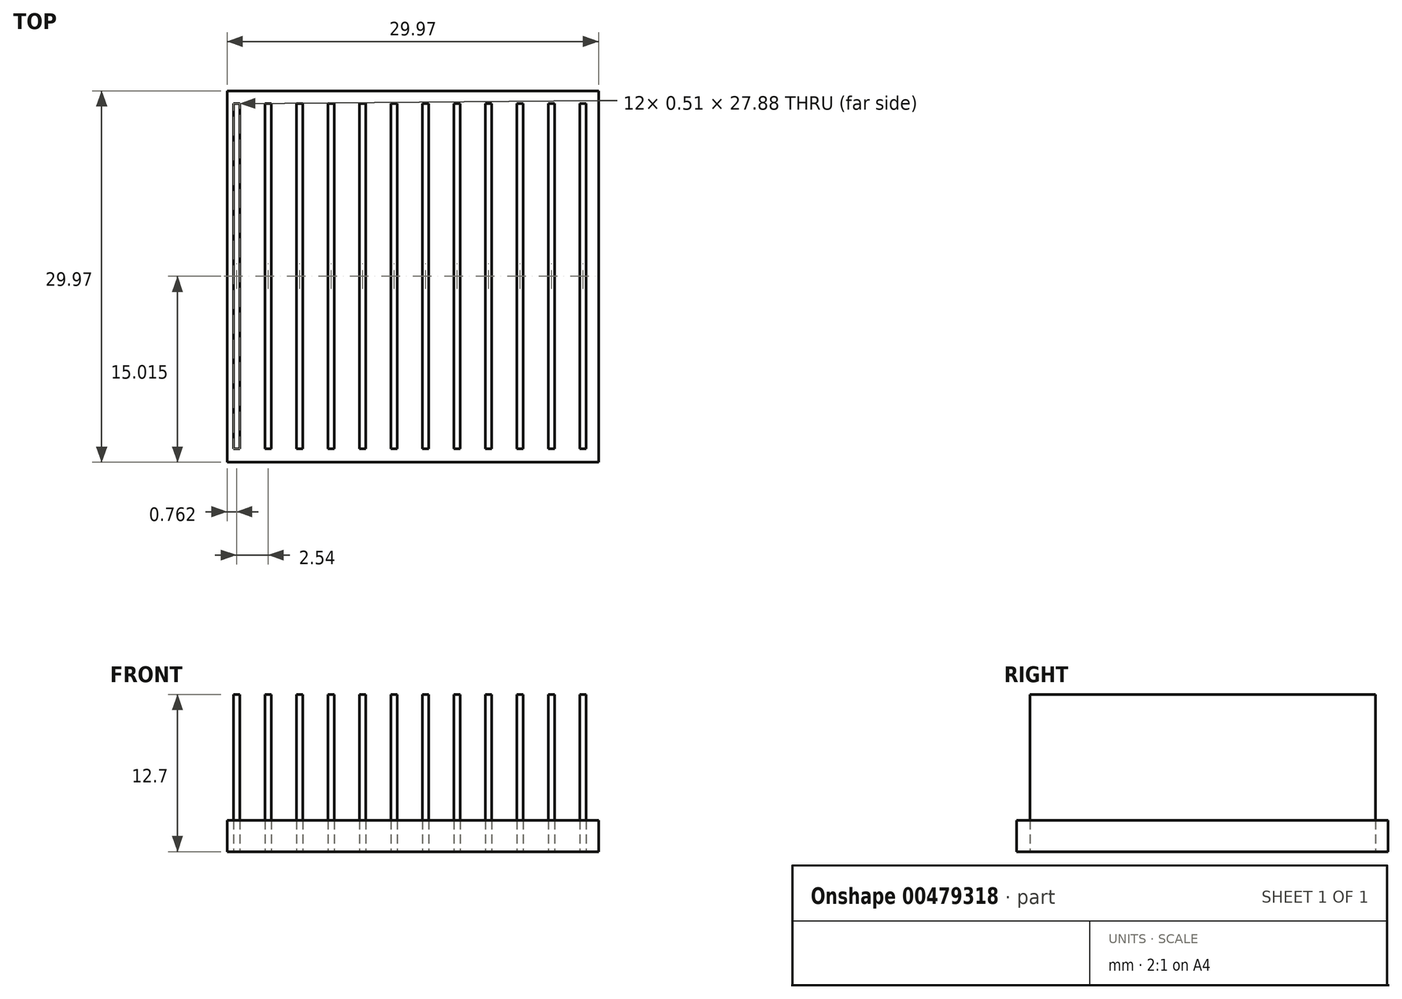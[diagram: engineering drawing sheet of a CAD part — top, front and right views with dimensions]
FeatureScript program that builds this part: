
annotation { "Feature Type Name" : "Feature", "Feature Type Description" : "" }
export const myFeature = defineFeature(function(context is Context, id is Id, definition is map)
    precondition{}
    {
        {
            var Q0;
            Q0=qCreatedBy(makeId("Top.planeOp"),FACE);
            var sketch = newSketch(context, id + "F0", { "sketchPlane" : qUnion([Q0])});
            skLineSegment(sketch, "E0.bottom", {"start": v(0, 0) * mm, "end": v(29.97, 0) * mm});
            skLineSegment(sketch, "E0.top", {"start": v(0, 29.97) * mm, "end": v(29.97, 29.97) * mm});
            skLineSegment(sketch, "E0.left", {"start": v(0, 0) * mm, "end": v(0, 29.97) * mm});
            skLineSegment(sketch, "E0.right", {"start": v(29.97, 0) * mm, "end": v(29.97, 29.97) * mm});
            skLineSegment(sketch, "E1.bottom", {"start": v(0.5, 28.96) * mm, "end": v(1.02, 28.96) * mm});
            skLineSegment(sketch, "E1.top", {"start": v(0.5, 1.07) * mm, "end": v(1.02, 1.07) * mm});
            skLineSegment(sketch, "E1.left", {"start": v(0.5, 28.96) * mm, "end": v(0.5, 1.07) * mm});
            skLineSegment(sketch, "E1.right", {"start": v(1.02, 28.96) * mm, "end": v(1.02, 1.07) * mm});
            skLineSegment(sketch, "E2.1.0.0", {"start": v(3.56, 28.96) * mm, "end": v(3.56, 1.07) * mm});
            skLineSegment(sketch, "E2.1.0.1", {"start": v(3.05, 28.96) * mm, "end": v(3.05, 1.07) * mm});
            skLineSegment(sketch, "E2.1.0.2", {"start": v(3.05, 1.07) * mm, "end": v(3.56, 1.07) * mm});
            skLineSegment(sketch, "E2.1.0.3", {"start": v(3.05, 28.96) * mm, "end": v(3.56, 28.96) * mm});
            skLineSegment(sketch, "E2.2.0.0", {"start": v(6.1, 28.96) * mm, "end": v(6.1, 1.07) * mm});
            skLineSegment(sketch, "E2.2.0.1", {"start": v(5.59, 28.96) * mm, "end": v(5.59, 1.07) * mm});
            skLineSegment(sketch, "E2.2.0.2", {"start": v(5.59, 1.07) * mm, "end": v(6.1, 1.07) * mm});
            skLineSegment(sketch, "E2.2.0.3", {"start": v(5.59, 28.96) * mm, "end": v(6.1, 28.96) * mm});
            skLineSegment(sketch, "E2.3.0.0", {"start": v(8.64, 28.96) * mm, "end": v(8.64, 1.07) * mm});
            skLineSegment(sketch, "E2.3.0.1", {"start": v(8.13, 28.96) * mm, "end": v(8.13, 1.07) * mm});
            skLineSegment(sketch, "E2.3.0.2", {"start": v(8.13, 1.07) * mm, "end": v(8.64, 1.07) * mm});
            skLineSegment(sketch, "E2.3.0.3", {"start": v(8.13, 28.96) * mm, "end": v(8.64, 28.96) * mm});
            skLineSegment(sketch, "E2.4.0.0", {"start": v(11.18, 28.96) * mm, "end": v(11.18, 1.07) * mm});
            skLineSegment(sketch, "E2.4.0.1", {"start": v(10.67, 28.96) * mm, "end": v(10.67, 1.07) * mm});
            skLineSegment(sketch, "E2.4.0.2", {"start": v(10.67, 1.07) * mm, "end": v(11.18, 1.07) * mm});
            skLineSegment(sketch, "E2.4.0.3", {"start": v(10.67, 28.96) * mm, "end": v(11.18, 28.96) * mm});
            skLineSegment(sketch, "E2.5.0.0", {"start": v(13.72, 28.96) * mm, "end": v(13.72, 1.07) * mm});
            skLineSegment(sketch, "E2.5.0.1", {"start": v(13.2, 28.96) * mm, "end": v(13.2, 1.07) * mm});
            skLineSegment(sketch, "E2.5.0.2", {"start": v(13.2, 1.07) * mm, "end": v(13.72, 1.07) * mm});
            skLineSegment(sketch, "E2.5.0.3", {"start": v(13.2, 28.96) * mm, "end": v(13.72, 28.96) * mm});
            skLineSegment(sketch, "E2.6.0.0", {"start": v(16.26, 28.96) * mm, "end": v(16.26, 1.07) * mm});
            skLineSegment(sketch, "E2.6.0.1", {"start": v(15.75, 28.96) * mm, "end": v(15.75, 1.07) * mm});
            skLineSegment(sketch, "E2.6.0.2", {"start": v(15.75, 1.07) * mm, "end": v(16.26, 1.07) * mm});
            skLineSegment(sketch, "E2.6.0.3", {"start": v(15.75, 28.96) * mm, "end": v(16.26, 28.96) * mm});
            skLineSegment(sketch, "E2.7.0.0", {"start": v(18.8, 28.96) * mm, "end": v(18.8, 1.07) * mm});
            skLineSegment(sketch, "E2.7.0.1", {"start": v(18.29, 28.96) * mm, "end": v(18.29, 1.07) * mm});
            skLineSegment(sketch, "E2.7.0.2", {"start": v(18.29, 1.07) * mm, "end": v(18.8, 1.07) * mm});
            skLineSegment(sketch, "E2.7.0.3", {"start": v(18.29, 28.96) * mm, "end": v(18.8, 28.96) * mm});
            skLineSegment(sketch, "E2.8.0.0", {"start": v(21.34, 28.96) * mm, "end": v(21.34, 1.07) * mm});
            skLineSegment(sketch, "E2.8.0.1", {"start": v(20.83, 28.96) * mm, "end": v(20.83, 1.07) * mm});
            skLineSegment(sketch, "E2.8.0.2", {"start": v(20.83, 1.07) * mm, "end": v(21.34, 1.07) * mm});
            skLineSegment(sketch, "E2.8.0.3", {"start": v(20.83, 28.96) * mm, "end": v(21.34, 28.96) * mm});
            skLineSegment(sketch, "E2.9.0.0", {"start": v(23.88, 28.96) * mm, "end": v(23.88, 1.07) * mm});
            skLineSegment(sketch, "E2.9.0.1", {"start": v(23.37, 28.96) * mm, "end": v(23.37, 1.07) * mm});
            skLineSegment(sketch, "E2.9.0.2", {"start": v(23.37, 1.07) * mm, "end": v(23.88, 1.07) * mm});
            skLineSegment(sketch, "E2.9.0.3", {"start": v(23.37, 28.96) * mm, "end": v(23.88, 28.96) * mm});
            skLineSegment(sketch, "E2.direction1", {"start": v(1.02, 1.07) * mm, "end": v(3.56, 1.07) * mm, "construction": true});
            skLineSegment(sketch, "E3.1.0.0", {"start": v(25.9, 28.96) * mm, "end": v(25.9, 1.07) * mm});
            skLineSegment(sketch, "E3.1.0.1", {"start": v(26.42, 28.96) * mm, "end": v(26.42, 1.07) * mm});
            skLineSegment(sketch, "E3.1.0.2", {"start": v(25.9, 1.07) * mm, "end": v(26.42, 1.07) * mm});
            skLineSegment(sketch, "E3.1.0.3", {"start": v(25.9, 28.96) * mm, "end": v(26.42, 28.96) * mm});
            skLineSegment(sketch, "E3.2.0.0", {"start": v(28.45, 28.96) * mm, "end": v(28.45, 1.07) * mm});
            skLineSegment(sketch, "E3.2.0.1", {"start": v(28.96, 28.96) * mm, "end": v(28.96, 1.07) * mm});
            skLineSegment(sketch, "E3.2.0.2", {"start": v(28.45, 1.07) * mm, "end": v(28.96, 1.07) * mm});
            skLineSegment(sketch, "E3.2.0.3", {"start": v(28.45, 28.96) * mm, "end": v(28.96, 28.96) * mm});
            skLineSegment(sketch, "E3.direction1", {"start": v(23.37, 1.07) * mm, "end": v(25.9, 1.07) * mm, "construction": true});
            skSolve(sketch);
        }
        {
            var Q0;
            Q0=makeQuery(id+"F0.imprint","IMPRINT",FACE,{"disambiguationData":[TD([[makeQuery(id+"F0.imprint","IMPRINT",EDGE,{"derivedFrom":sQuery(id+"F0.wireOp",EDGE,"E1.bottom")}),-1.0]])]});
            var Q1;
            Q1=makeQuery(id+"F0.imprint","IMPRINT",FACE,{"disambiguationData":[TD([[makeQuery(id+"F0.imprint","IMPRINT",EDGE,{"derivedFrom":sQuery(id+"F0.wireOp",EDGE,"E2.1.0.0")}),-1.0]])]});
            var Q2;
            Q2=makeQuery(id+"F0.imprint","IMPRINT",FACE,{"disambiguationData":[TD([[makeQuery(id+"F0.imprint","IMPRINT",EDGE,{"derivedFrom":sQuery(id+"F0.wireOp",EDGE,"E2.2.0.0")}),-1.0]])]});
            var Q3;
            Q3=makeQuery(id+"F0.imprint","IMPRINT",FACE,{"disambiguationData":[TD([[makeQuery(id+"F0.imprint","IMPRINT",EDGE,{"derivedFrom":sQuery(id+"F0.wireOp",EDGE,"E2.3.0.0")}),-1.0]])]});
            var Q4;
            Q4=makeQuery(id+"F0.imprint","IMPRINT",FACE,{"disambiguationData":[TD([[makeQuery(id+"F0.imprint","IMPRINT",EDGE,{"derivedFrom":sQuery(id+"F0.wireOp",EDGE,"E2.4.0.0")}),-1.0]])]});
            var Q5;
            Q5=makeQuery(id+"F0.imprint","IMPRINT",FACE,{"disambiguationData":[TD([[makeQuery(id+"F0.imprint","IMPRINT",EDGE,{"derivedFrom":sQuery(id+"F0.wireOp",EDGE,"E2.5.0.0")}),-1.0]])]});
            var Q6;
            Q6=makeQuery(id+"F0.imprint","IMPRINT",FACE,{"disambiguationData":[TD([[makeQuery(id+"F0.imprint","IMPRINT",EDGE,{"derivedFrom":sQuery(id+"F0.wireOp",EDGE,"E2.6.0.0")}),-1.0]])]});
            var Q7;
            Q7=makeQuery(id+"F0.imprint","IMPRINT",FACE,{"disambiguationData":[TD([[makeQuery(id+"F0.imprint","IMPRINT",EDGE,{"derivedFrom":sQuery(id+"F0.wireOp",EDGE,"E2.7.0.0")}),-1.0]])]});
            var Q8;
            Q8=makeQuery(id+"F0.imprint","IMPRINT",FACE,{"disambiguationData":[TD([[makeQuery(id+"F0.imprint","IMPRINT",EDGE,{"derivedFrom":sQuery(id+"F0.wireOp",EDGE,"E2.8.0.0")}),-1.0]])]});
            var Q9;
            Q9=makeQuery(id+"F0.imprint","IMPRINT",FACE,{"disambiguationData":[TD([[makeQuery(id+"F0.imprint","IMPRINT",EDGE,{"derivedFrom":sQuery(id+"F0.wireOp",EDGE,"E2.9.0.0")}),-1.0]])]});
            var Q10;
            Q10=makeQuery(id+"F0.imprint","IMPRINT",FACE,{"disambiguationData":[TD([[makeQuery(id+"F0.imprint","IMPRINT",EDGE,{"derivedFrom":sQuery(id+"F0.wireOp",EDGE,"E3.1.0.0")}),1.0]])]});
            var Q11;
            Q11=makeQuery(id+"F0.imprint","IMPRINT",FACE,{"disambiguationData":[TD([[makeQuery(id+"F0.imprint","IMPRINT",EDGE,{"derivedFrom":sQuery(id+"F0.wireOp",EDGE,"E3.2.0.0")}),1.0]])]});
            extrude(context, id + "F1", {"entities" : qUnion([Q0, Q1, Q2, Q3, Q4, Q5, Q6, Q7, Q8, Q9, Q10, Q11]), "depth" : 12.7 * mm});
        }
        {
            var Q0;
            Q0=makeQuery(id+"F0.imprint","IMPRINT",FACE,{"disambiguationData":[TD([[makeQuery(id+"F0.imprint","IMPRINT",EDGE,{"derivedFrom":sQuery(id+"F0.wireOp",EDGE,"E0.bottom")}),1.0]])]});
            extrude(context, id + "F2", {"entities" : qUnion([Q0]), "depth" : 2.54 * mm});
        }
    });
